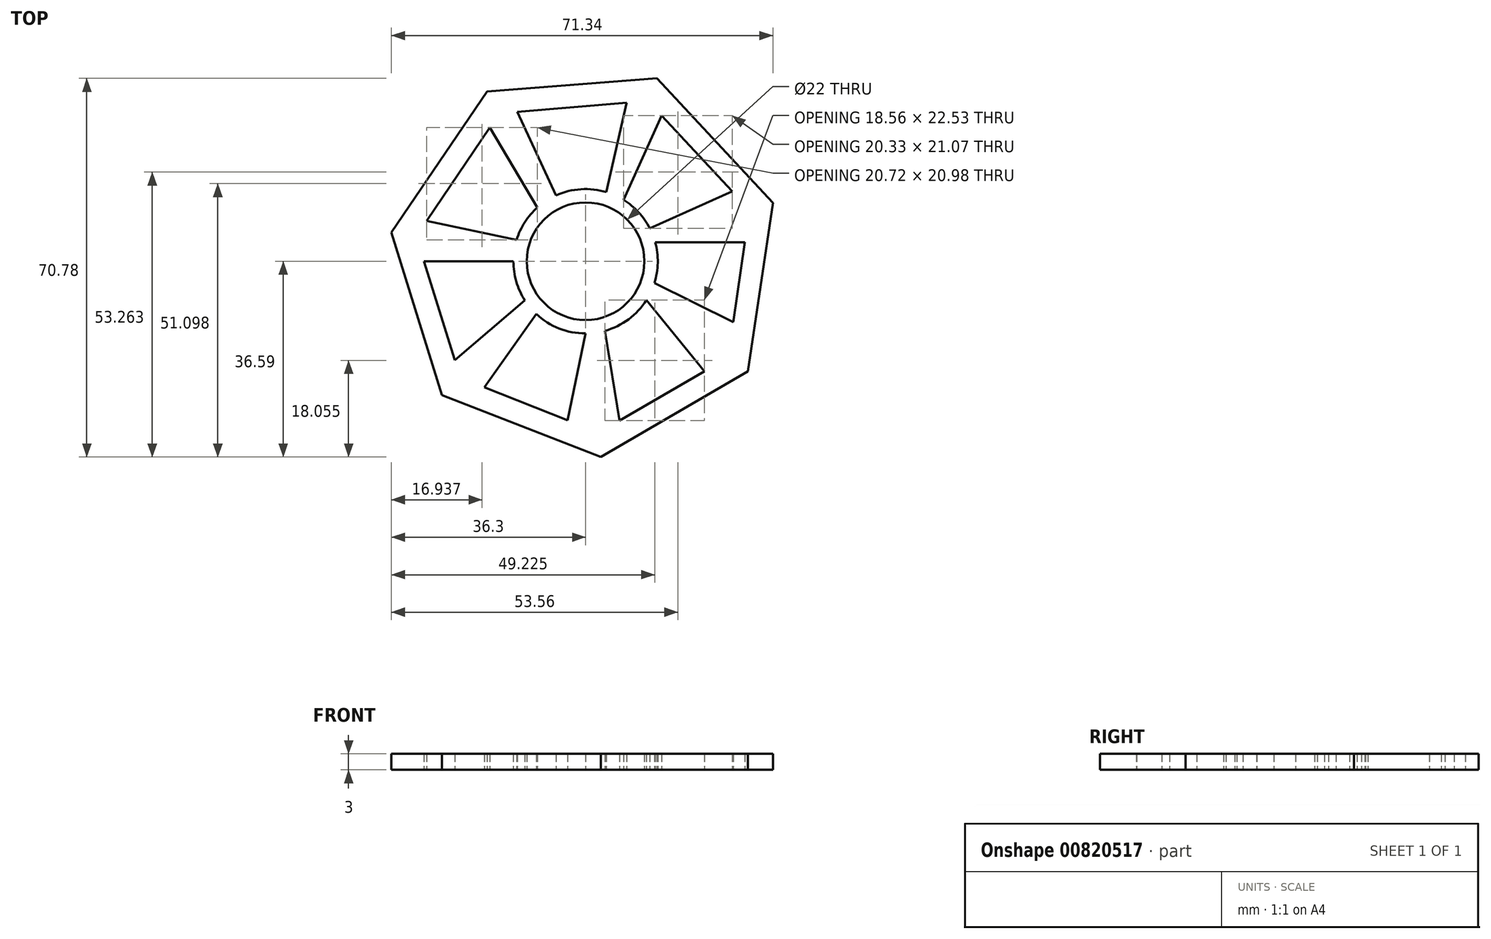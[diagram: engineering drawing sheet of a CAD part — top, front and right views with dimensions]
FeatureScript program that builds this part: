
annotation { "Feature Type Name" : "Feature", "Feature Type Description" : "" }
export const myFeature = defineFeature(function(context is Context, id is Id, definition is map)
    precondition{}
    {
        {
            var Q0;
            Q0=qCreatedBy(makeId("Top.planeOp"),FACE);
            var sketch = newSketch(context, id + "F0", { "sketchPlane" : qUnion([Q0])});
            skCircle(sketch, "E0", {"center": v(0, 0) * mm, "radius": 11 * mm});
            skArc(sketch, "E1", {"start": v(-9.2, -9.87) * mm, "mid": v(-4.95, -12.56) * mm, "end": v(0, -13.5) * mm});
            skLineSegment(sketch, "E2.0", {"start": v(30.37, -20.6) * mm, "end": v(2.84, -36.59) * mm});
            skLineSegment(sketch, "E2.1", {"start": v(2.84, -36.59) * mm, "end": v(-26.84, -25.03) * mm});
            skLineSegment(sketch, "E2.2", {"start": v(-26.84, -25.03) * mm, "end": v(-36.3, 5.37) * mm});
            skLineSegment(sketch, "E2.3", {"start": v(-36.3, 5.37) * mm, "end": v(-18.43, 31.73) * mm});
            skLineSegment(sketch, "E2.4", {"start": v(-18.43, 31.73) * mm, "end": v(13.32, 34.2) * mm});
            skLineSegment(sketch, "E2.5", {"start": v(13.32, 34.2) * mm, "end": v(35.04, 10.9) * mm});
            skLineSegment(sketch, "E2.6", {"start": v(35.04, 10.9) * mm, "end": v(30.37, -20.6) * mm});
            skPoint(sketch, "E2.0.midPoint", {"position": v(16.6, -28.59) * mm});
            skLineSegment(sketch, "E3", {"start": v(-17.89, 25) * mm, "end": v(-23.78, 16.3) * mm});
            skLineSegment(sketch, "E4", {"start": v(-30.2, 0) * mm, "end": v(-24.43, -18.52) * mm});
            skLineSegment(sketch, "E5", {"start": v(-18.92, -23.6) * mm, "end": v(-3.4, -29.73) * mm});
            skLineSegment(sketch, "E6", {"start": v(6.35, -29.8) * mm, "end": v(22.2, -20.6) * mm});
            skLineSegment(sketch, "E7", {"start": v(27.6, -11.37) * mm, "end": v(29.8, 3.56) * mm});
            skLineSegment(sketch, "E8", {"start": v(27.43, 13.05) * mm, "end": v(14.22, 27.2) * mm});
            skLineSegment(sketch, "E9", {"start": v(7.7, 29.63) * mm, "end": v(-12.76, 27.95) * mm});
            skLineSegment(sketch, "E10.trimOffspring", {"start": v(-23.95, 16.06) * mm, "end": v(-29.72, 7.54) * mm});
            skLineSegment(sketch, "E11", {"start": v(-17.89, 25) * mm, "end": v(-9, 10.06) * mm});
            skLineSegment(sketch, "E12", {"start": v(-12.76, 27.95) * mm, "end": v(-5.5, 12.33) * mm});
            skLineSegment(sketch, "E13", {"start": v(-29.72, 7.54) * mm, "end": v(-12.89, 4.02) * mm});
            skLineSegment(sketch, "E14", {"start": v(-13.5, 0) * mm, "end": v(-30.2, 0) * mm});
            skLineSegment(sketch, "E15", {"start": v(-11.36, -7.3) * mm, "end": v(-24.43, -18.52) * mm});
            skLineSegment(sketch, "E16", {"start": v(-9.2, -9.87) * mm, "end": v(-18.92, -23.6) * mm});
            skLineSegment(sketch, "E17", {"start": v(0, -13.5) * mm, "end": v(-3.4, -29.73) * mm});
            skLineSegment(sketch, "E18", {"start": v(3.65, -13) * mm, "end": v(6.35, -29.8) * mm});
            skLineSegment(sketch, "E19", {"start": v(11.38, -7.27) * mm, "end": v(22.2, -20.6) * mm});
            skLineSegment(sketch, "E20", {"start": v(12.88, -4.06) * mm, "end": v(27.6, -11.37) * mm});
            skLineSegment(sketch, "E21", {"start": v(14.22, 27.2) * mm, "end": v(7.1, 11.49) * mm});
            skLineSegment(sketch, "E22", {"start": v(7.7, 29.63) * mm, "end": v(3.9, 12.93) * mm});
            skLineSegment(sketch, "E23", {"start": v(27.43, 13.05) * mm, "end": v(12.02, 6.14) * mm});
            skLineSegment(sketch, "E24", {"start": v(13.02, 3.56) * mm, "end": v(29.8, 3.56) * mm});
            skPoint(sketch, "E25.orphan", {"position": v(-31.66, 4.69) * mm});
            skPoint(sketch, "E26.start.orphan", {"position": v(-4.45, 10.06) * mm});
            skPoint(sketch, "E27.orphan", {"position": v(-12.89, 0) * mm});
            skPoint(sketch, "E28.orphan", {"position": v(-31.66, 0) * mm});
            skArc(sketch, "E29.trimOffspring", {"start": v(3.65, -13) * mm, "mid": v(8.04, -10.85) * mm, "end": v(11.38, -7.27) * mm});
            skArc(sketch, "E30.trimOffspring", {"start": v(12.88, -4.06) * mm, "mid": v(13.5, -0.26) * mm, "end": v(13.02, 3.56) * mm});
            skArc(sketch, "E31.trimOffspring", {"start": v(12.02, 6.14) * mm, "mid": v(9.93, 9.15) * mm, "end": v(7.1, 11.49) * mm});
            skArc(sketch, "E32.trimOffspring", {"start": v(-13.5, 0) * mm, "mid": v(-12.95, -3.8) * mm, "end": v(-11.36, -7.3) * mm});
            skArc(sketch, "E33.trimOffspring", {"start": v(3.9, 12.93) * mm, "mid": v(-0.86, 13.47) * mm, "end": v(-5.5, 12.33) * mm});
            skArc(sketch, "E34.trimOffspring", {"start": v(-9, 10.06) * mm, "mid": v(-11.35, 7.3) * mm, "end": v(-12.89, 4.02) * mm});
            skLineSegment(sketch, "E35", {"start": v(-23.95, 16.06) * mm, "end": v(-23.78, 16.3) * mm});
            skSolve(sketch);
        }
        {
            var Q0;
            Q0 = qSketchRegion(id + "F0", true);
            extrude(context, id + "F1", {"entities" : qUnion([Q0]), "depth" : 3 * mm, "offsetDistance" : 25 * mm});
        }
    });
